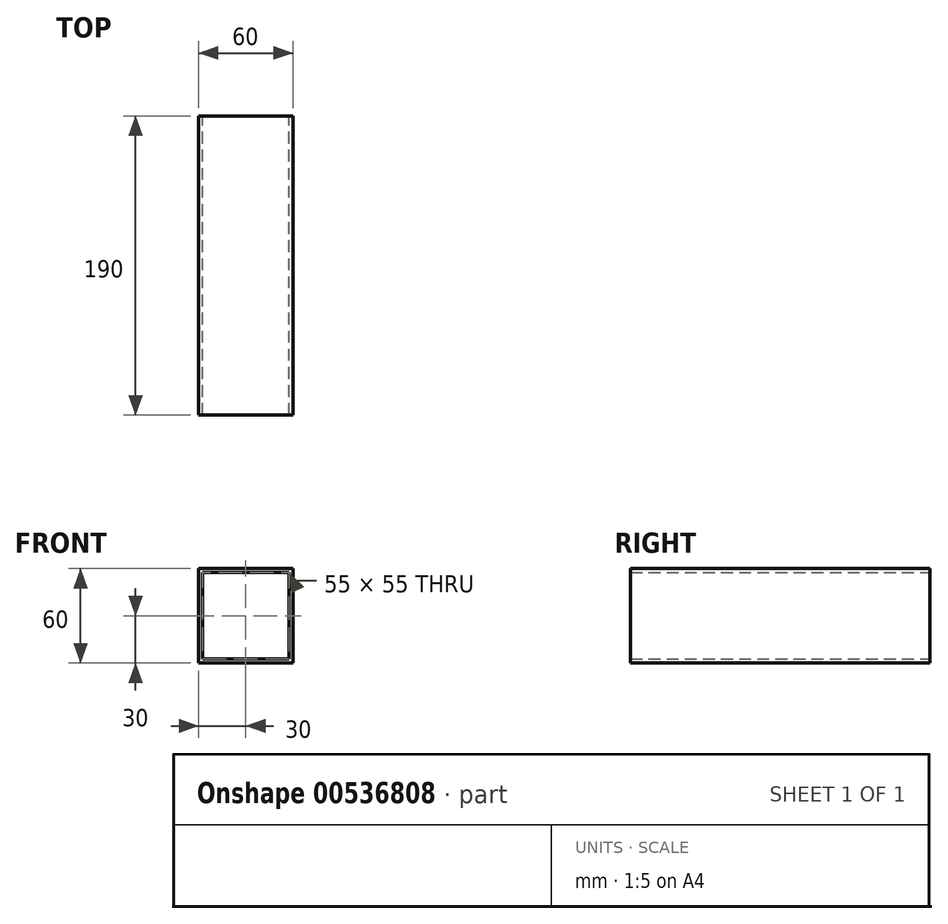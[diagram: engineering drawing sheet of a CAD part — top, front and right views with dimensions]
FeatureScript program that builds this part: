
annotation { "Feature Type Name" : "Feature", "Feature Type Description" : "" }
export const myFeature = defineFeature(function(context is Context, id is Id, definition is map)
    precondition{}
    {
        {
            var Q0;
            Q0=qCreatedBy(makeId("Front.planeOp"),FACE);
            var sketch = newSketch(context, id + "F0", { "sketchPlane" : qUnion([Q0])});
            skLineSegment(sketch, "E0.bottom", {"start": v(-30, -30) * mm, "end": v(30, -30) * mm});
            skLineSegment(sketch, "E0.top", {"start": v(-30, 30) * mm, "end": v(30, 30) * mm});
            skLineSegment(sketch, "E0.left", {"start": v(-30, -30) * mm, "end": v(-30, 30) * mm});
            skLineSegment(sketch, "E0.right", {"start": v(30, -30) * mm, "end": v(30, 30) * mm});
            skPoint(sketch, "E0.middle", {"position": v(0, 0) * mm});
            skLineSegment(sketch, "E1.bottom", {"start": v(-27.5, -27.5) * mm, "end": v(27.5, -27.5) * mm});
            skLineSegment(sketch, "E1.top", {"start": v(-27.5, 27.5) * mm, "end": v(27.5, 27.5) * mm});
            skLineSegment(sketch, "E1.left", {"start": v(-27.5, -27.5) * mm, "end": v(-27.5, 27.5) * mm});
            skLineSegment(sketch, "E1.right", {"start": v(27.5, -27.5) * mm, "end": v(27.5, 27.5) * mm});
            skSolve(sketch);
        }
        {
            var Q0;
            Q0=makeQuery(id+"F0.imprint","IMPRINT",FACE,{"disambiguationData":[TD([[makeQuery(id+"F0.imprint","IMPRINT",EDGE,{"derivedFrom":sQuery(id+"F0.wireOp",EDGE,"E0.bottom")}),1.0]])]});
            extrude(context, id + "F1", {"entities" : qUnion([Q0]), "depth" : 190 * mm, "offsetDistance" : 25 * mm});
        }
    });
